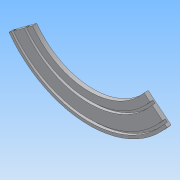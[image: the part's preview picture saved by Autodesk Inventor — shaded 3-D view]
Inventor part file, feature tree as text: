
AUTODESK INVENTOR PART (.ipt)
format: ipt  version: 2013 (Build 170138000, 138)  size: 139,776 bytes
history: native  units: in
note: dims shown in document units (in); Inventor stores cm internally (conversion verified against a paired STEP export)
features: extrude x2, plane x1, other x1, reference x1, sketch x1
ambient origin geometry x8: Origin, YZ Plane, XZ Plane, XY Plane, X Axis, Y Axis, Z Axis, Center Point
bodies: Solid1 (feature_tree)
feature tree (6):
  plane  "Work Plane1"
  other  "ThermoBulbBorder"
  extrude  "Extrusion2"  Depth=2.5in
  extrude  "Extrusion3"  Depth=2.5in
  reference  "Reference2"
  sketch  "Sketch2"  dims[d0=24.0in d5=2.5in d6=2.5in d7=33.0in d8=0.48in d9=0.48in d10=2.25in d11=1.29in d12=6.0in d13=0.71in d14=0.0in d15=0.48in d17=0.5in d18=2.25in d19=0.48in d20=0.5in d21=0.0in]
